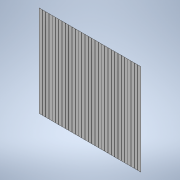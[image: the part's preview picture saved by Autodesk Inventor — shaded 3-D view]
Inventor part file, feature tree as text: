
AUTODESK INVENTOR PART (.ipt)
format: ipt  version: 2021 (Build 250183000, 183)  size: 221,184 bytes
history: native  units: in
note: dims shown in document units (in); Inventor stores cm internally (conversion verified against a paired STEP export)
features: extrude x3, sketch x3, pattern_linear x1, projected_geometry x1
ambient origin geometry x8: Origin, YZ Plane, XZ Plane, XY Plane, X Axis, Y Axis, Z Axis, Center Point
bodies: Solid1 (feature_tree)
feature tree (8):
  extrude  "Extrusion1"  Depth=3.0in
  extrude  "Extrusion2"  Depth=0.1in
  pattern_linear  "Rectangular Pattern1"  Count1=31 Spacing1=0.108in
  extrude  "Extrusion3"  Depth=0.108in TaperAngle=0.0deg
  sketch  "Sketch1"  dims[d0=4.0in d1=3.0in]
  sketch  "Sketch2"  dims[d2=0.04in d3=0.0in d4=0.1in]
  projected_geometry  "Projected Loop1"
  sketch  "Sketch3"  dims[d5=0.0015in d6=0.0in d7=12.2047in d9=0.108in d10=1.0in d11=0.0in]
